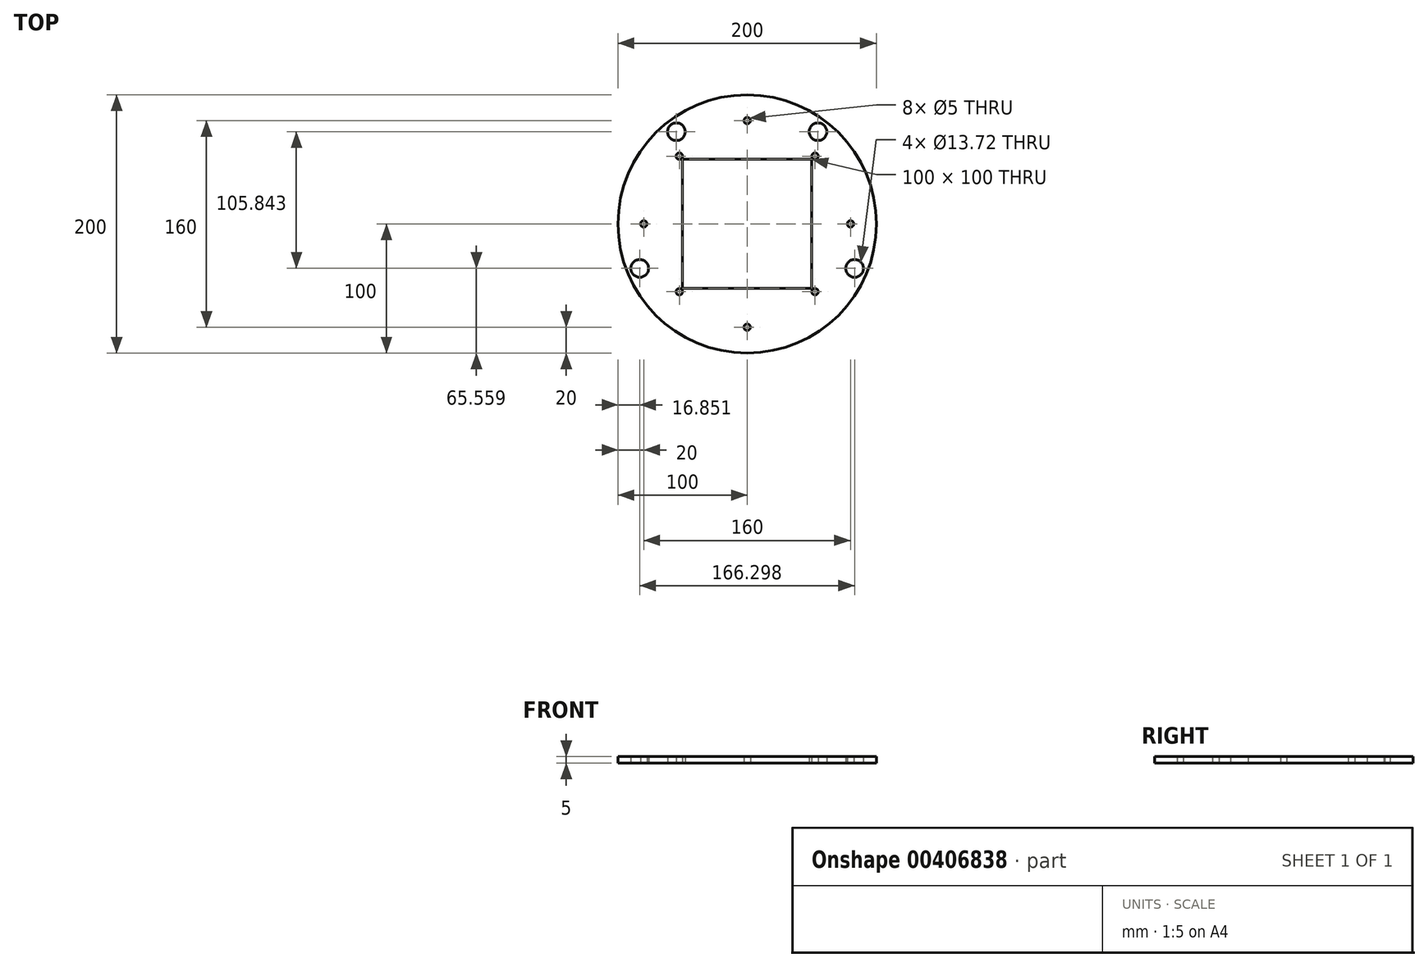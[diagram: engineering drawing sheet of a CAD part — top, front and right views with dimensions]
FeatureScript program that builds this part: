
annotation { "Feature Type Name" : "Feature", "Feature Type Description" : "" }
export const myFeature = defineFeature(function(context is Context, id is Id, definition is map)
    precondition{}
    {
        {
            var Q0;
            Q0=qCreatedBy(makeId("Top.planeOp"),FACE);
            var sketch = newSketch(context, id + "F0", { "sketchPlane" : qUnion([Q0])});
            skPoint(sketch, "E0.middle", {"position": v(0, 0) * mm});
            skCircle(sketch, "E1", {"center": v(0, 0) * mm, "radius": 100 * mm});
            skLineSegment(sketch, "E2.bottom", {"start": v(50, 50) * mm, "end": v(-50, 50) * mm});
            skLineSegment(sketch, "E2.top", {"start": v(50, -50) * mm, "end": v(-50, -50) * mm});
            skLineSegment(sketch, "E2.left", {"start": v(50, 50) * mm, "end": v(50, -50) * mm});
            skLineSegment(sketch, "E2.right", {"start": v(-50, 50) * mm, "end": v(-50, -50) * mm});
            skCircle(sketch, "E3", {"center": v(-80, 0) * mm, "radius": 2.5 * mm});
            skCircle(sketch, "E4.1.0", {"center": v(0, -80) * mm, "radius": 2.5 * mm});
            skCircle(sketch, "E4.2.0", {"center": v(80, 0) * mm, "radius": 2.5 * mm});
            skCircle(sketch, "E4.3.0", {"center": v(0, 80) * mm, "radius": 2.5 * mm});
            skLineSegment(sketch, "E5.bottom", {"start": v(60, -60) * mm, "end": v(-60, -60) * mm, "construction": true});
            skLineSegment(sketch, "E5.top", {"start": v(60, 60) * mm, "end": v(-60, 60) * mm, "construction": true});
            skLineSegment(sketch, "E5.left", {"start": v(60, -60) * mm, "end": v(60, 60) * mm, "construction": true});
            skLineSegment(sketch, "E5.right", {"start": v(-60, -60) * mm, "end": v(-60, 60) * mm, "construction": true});
            skCircle(sketch, "E6", {"center": v(-83.15, -34.44) * mm, "radius": 6.86 * mm});
            skLineSegment(sketch, "E7", {"start": v(0, 0) * mm, "end": v(-83.15, -34.44) * mm, "construction": true});
            skCircle(sketch, "E8.1.0", {"center": v(-54.79, 71.4) * mm, "radius": 6.86 * mm});
            skCircle(sketch, "E8.2.0", {"center": v(54.79, 71.4) * mm, "radius": 6.86 * mm});
            skCircle(sketch, "E8.3.0", {"center": v(83.15, -34.44) * mm, "radius": 6.86 * mm});
            skLineSegment(sketch, "E8.anchor2", {"start": v(0, 0) * mm, "end": v(83.15, -34.44) * mm, "construction": true});
            skCircle(sketch, "E9", {"center": v(-52.5, 52.5) * mm, "radius": 2.5 * mm});
            skCircle(sketch, "E10.1.0", {"center": v(-52.5, -52.5) * mm, "radius": 2.5 * mm});
            skCircle(sketch, "E10.2.0", {"center": v(52.5, -52.5) * mm, "radius": 2.5 * mm});
            skCircle(sketch, "E10.3.0", {"center": v(52.5, 52.5) * mm, "radius": 2.5 * mm});
            skSolve(sketch);
        }
        {
            var Q0;
            Q0 = qSketchRegion(id + "F0", true);
            extrude(context, id + "F1", {"entities" : qUnion([Q0]), "depth" : 5 * mm});
        }
    });
